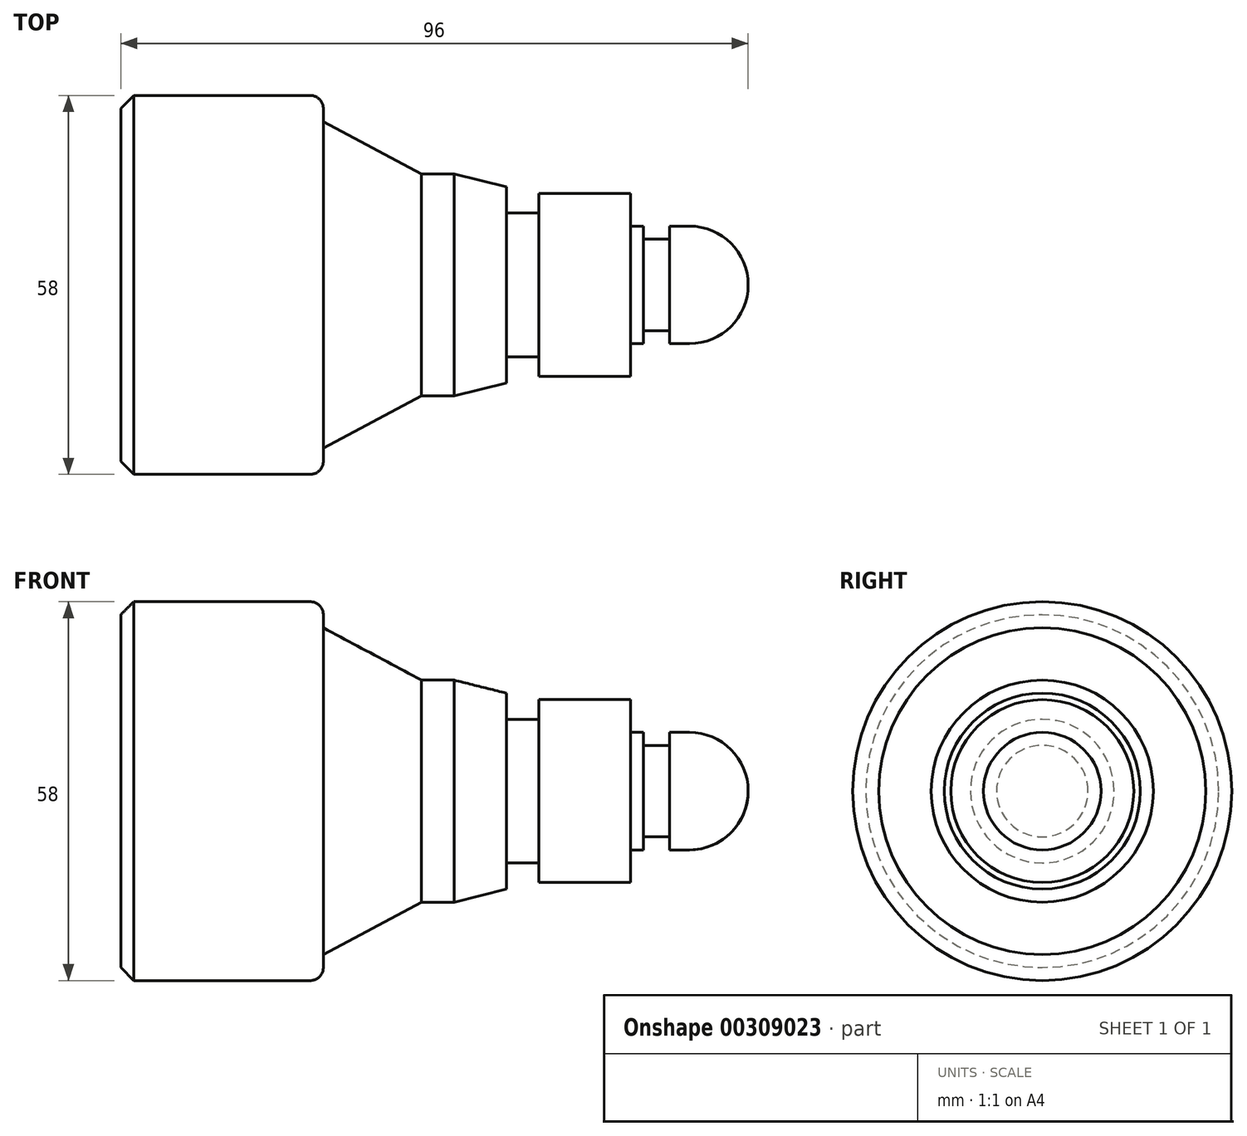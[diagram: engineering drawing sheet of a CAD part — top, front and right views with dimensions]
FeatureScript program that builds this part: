
annotation { "Feature Type Name" : "Feature", "Feature Type Description" : "" }
export const myFeature = defineFeature(function(context is Context, id is Id, definition is map)
    precondition{}
    {
        {
            var Q0;
            Q0=qCreatedBy(makeId("Front.planeOp"),FACE);
            var sketch = newSketch(context, id + "F0", { "sketchPlane" : qUnion([Q0])});
            skLineSegment(sketch, "E0", {"start": v(0, 0) * mm, "end": v(0, 29) * mm});
            skLineSegment(sketch, "E1", {"start": v(0, 29) * mm, "end": v(31, 29) * mm});
            skLineSegment(sketch, "E2", {"start": v(46, 17) * mm, "end": v(51, 17) * mm});
            skLineSegment(sketch, "E3", {"start": v(51, 17) * mm, "end": v(59, 15) * mm});
            skLineSegment(sketch, "E4", {"start": v(59, 15) * mm, "end": v(59, 11) * mm});
            skLineSegment(sketch, "E5", {"start": v(59, 11) * mm, "end": v(64, 11) * mm});
            skLineSegment(sketch, "E6", {"start": v(64, 11) * mm, "end": v(64, 14) * mm});
            skLineSegment(sketch, "E7", {"start": v(64, 14) * mm, "end": v(78, 14) * mm});
            skLineSegment(sketch, "E8", {"start": v(80, 7) * mm, "end": v(84, 7) * mm});
            skLineSegment(sketch, "E9", {"start": v(84, 7) * mm, "end": v(84, 9) * mm});
            skLineSegment(sketch, "E10", {"start": v(84, 9) * mm, "end": v(96, 9) * mm});
            skLineSegment(sketch, "E11", {"start": v(96, 9) * mm, "end": v(96, 0) * mm});
            skLineSegment(sketch, "E12", {"start": v(31, 29) * mm, "end": v(31, 25) * mm});
            skLineSegment(sketch, "E13", {"start": v(31, 25) * mm, "end": v(46, 17) * mm});
            skLineSegment(sketch, "E14", {"start": v(78, 14) * mm, "end": v(78, 9) * mm});
            skLineSegment(sketch, "E15", {"start": v(78, 9) * mm, "end": v(80, 9) * mm});
            skLineSegment(sketch, "E16", {"start": v(80, 9) * mm, "end": v(80, 7) * mm});
            skLineSegment(sketch, "E17", {"start": v(0, 0) * mm, "end": v(96, 0) * mm});
            skLineSegment(sketch, "E18", {"start": v(0, 0) * mm, "end": v(96, 0) * mm, "construction": true});
            skSolve(sketch);
        }
        {
            var Q0;
            Q0=makeQuery(id+"F0.imprint","IMPRINT",FACE,{"disambiguationData":[TD([[makeQuery(id+"F0.imprint","IMPRINT",EDGE,{"derivedFrom":sQuery(id+"F0.wireOp",EDGE,"E0")}),-1.0]])]});
            var Q1;
            Q1=sQuery(id+"F0.wireOp",EDGE,"E17");
            revolve(context, id + "F1", {"entities" : qUnion([Q0]), "axis" : qUnion([Q1]), "revolveType" : RevolveType.FULL});
        }
        {
            var Q0;
            Q0=makeQuery(id+"F1.opRevolve","SWEPT_FACE",FACE,{"disambiguationData":[OSD([sQuery(id+"F0.wireOp",EDGE,"E0")])]});
            chamfer(context, id + "F2", {"entities" : qUnion([Q0]), "width" : 2 * mm, "tangentPropagation" : true});
        }
        {
            var Q0;
            Q0=makeQuery(id+"F1.opRevolve","SWEPT_EDGE",EDGE,{"disambiguationData":[OSD([sQuery(id+"F0.wireOp",EDGE,"E1"),sQuery(id+"F0.wireOp",EDGE,"E12")])]});
            fillet(context, id + "F3", {"entities" : qUnion([Q0]), "radius" : 2 * mm, "tangentPropagation" : true, "allowEdgeOverflow" : false});
        }
        {
            var Q0;
            Q0=makeQuery(id+"F1.opRevolve","SWEPT_EDGE",EDGE,{"disambiguationData":[OSD([sQuery(id+"F0.wireOp",EDGE,"E10"),sQuery(id+"F0.wireOp",EDGE,"E11")])]});
            fillet(context, id + "F4", {"entities" : qUnion([Q0]), "radius" : 9 * mm, "tangentPropagation" : true, "allowEdgeOverflow" : false});
        }
    });
